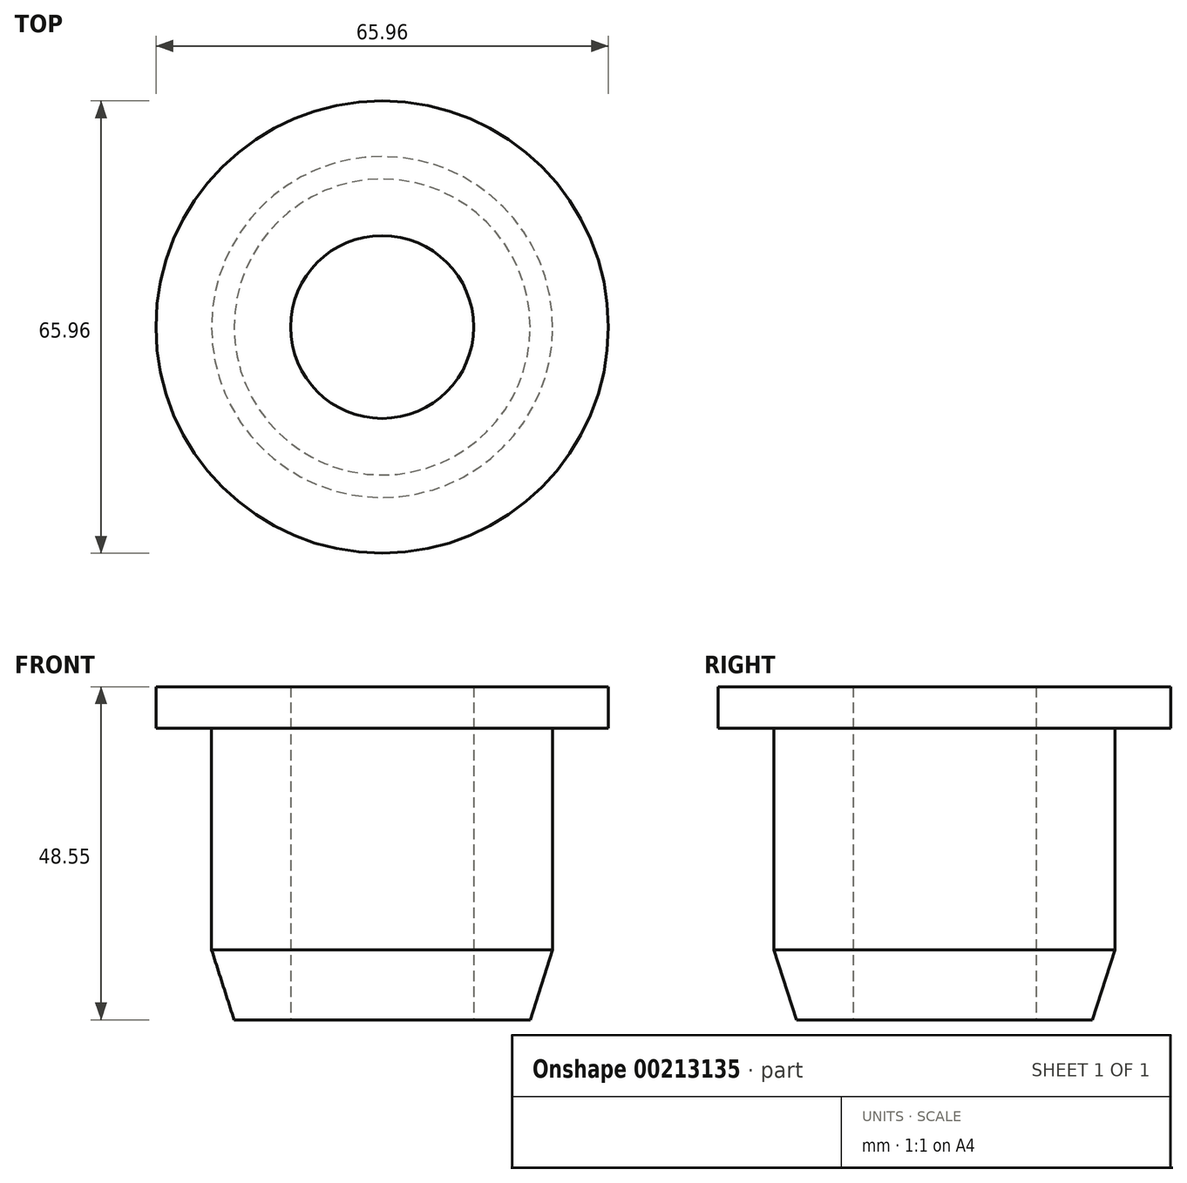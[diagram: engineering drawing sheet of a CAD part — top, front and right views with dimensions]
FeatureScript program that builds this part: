
annotation { "Feature Type Name" : "Feature", "Feature Type Description" : "" }
export const myFeature = defineFeature(function(context is Context, id is Id, definition is map)
    precondition{}
    {
        {
            var Q0;
            Q0=qCreatedBy(makeId("Front.planeOp"),FACE);
            var sketch = newSketch(context, id + "F0", { "sketchPlane" : qUnion([Q0])});
            skLineSegment(sketch, "E0", {"start": v(0, 0) * mm, "end": v(0, 48.55) * mm, "construction": true});
            skLineSegment(sketch, "E1", {"start": v(-32.98, 48.55) * mm, "end": v(-32.98, 42.52) * mm});
            skLineSegment(sketch, "E2", {"start": v(-32.98, 42.52) * mm, "end": v(-24.87, 42.52) * mm});
            skLineSegment(sketch, "E3", {"start": v(-24.87, 42.52) * mm, "end": v(-24.87, 10.19) * mm});
            skLineSegment(sketch, "E4", {"start": v(0, 0) * mm, "end": v(-21.58, 0) * mm, "construction": true});
            skLineSegment(sketch, "E5", {"start": v(-24.87, 10.19) * mm, "end": v(-21.58, 0) * mm});
            skLineSegment(sketch, "E6", {"start": v(-13.33, 0) * mm, "end": v(-21.58, 0) * mm});
            skLineSegment(sketch, "E7", {"start": v(-13.33, 0) * mm, "end": v(-13.33, 48.55) * mm});
            skLineSegment(sketch, "E8", {"start": v(-13.34, 48.55) * mm, "end": v(-32.98, 48.55) * mm});
            skPoint(sketch, "E9.endSnap0", {"position": v(-23.16, 48.55) * mm});
            skLineSegment(sketch, "E10", {"start": v(0, 22.5) * mm, "end": v(-13.33, 22.5) * mm, "construction": true});
            skSolve(sketch);
        }
        {
            var Q0;
            Q0=makeQuery(id+"F0.imprint","IMPRINT",FACE,{"disambiguationData":[TD([[makeQuery(id+"F0.imprint","IMPRINT",EDGE,{"derivedFrom":sQuery(id+"F0.wireOp",EDGE,"E3")}),1.0]])]});
            var Q1;
            Q1=makeQuery(id+"F0.imprint","IMPRINT",FACE,{"disambiguationData":[TD([[makeQuery(id+"F0.imprint","IMPRINT",EDGE,{"derivedFrom":sQuery(id+"F0.wireOp",EDGE,"E1")}),1.0]])]});
            var Q2;
            Q2=makeQuery(id+"F0.imprint","IMPRINT",FACE,{"disambiguationData":[TD([[makeQuery(id+"F0.imprint","IMPRINT",EDGE,{"derivedFrom":sQuery(id+"F0.wireOp",EDGE,"aDQXU6Wq-Cdum-vBUq-szyq-AXuKM0V0hB6W")}),-1.0]])]});
            var Q3;
            {var subQ1=sQuery(id+"F0.wireOp",EDGE,"uUD3JDk1-i4TZ-WyDG-QxaW-fDQCfXrNh4qW");Q3=makeQuery(id+"F0.imprint","IMPRINT",FACE,{"disambiguationData":[TD([[makeQuery(id+"F0.imprint","IMPRINT",EDGE,{"derivedFrom":subQ1}),1.0]])]});}
            var Q4;
            Q4=sQuery(id+"F0.wireOp",EDGE,"E0");
            revolve(context, id + "F1", {"entities" : qUnion([Q0, Q1, Q2, Q3]), "axis" : qUnion([Q4]), "revolveType" : RevolveType.FULL});
        }
    });
